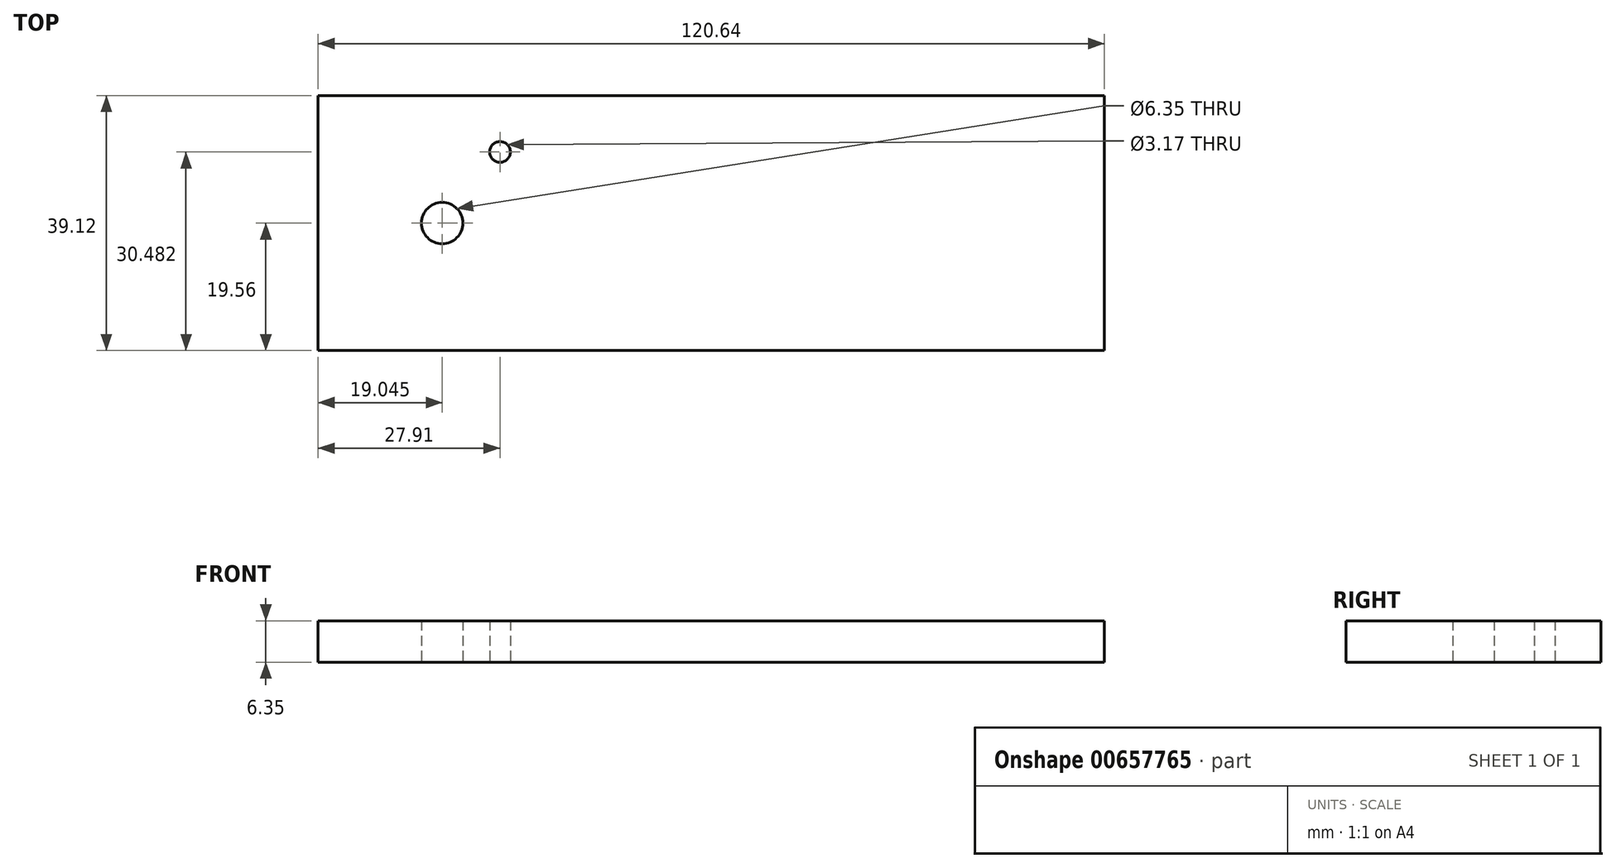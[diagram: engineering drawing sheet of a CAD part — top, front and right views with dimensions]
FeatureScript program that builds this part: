
annotation { "Feature Type Name" : "Feature", "Feature Type Description" : "" }
export const myFeature = defineFeature(function(context is Context, id is Id, definition is map)
    precondition{}
    {
        {
            var Q0;
            Q0=qCreatedBy(makeId("Top.planeOp"),FACE);
            var sketch = newSketch(context, id + "F0", { "sketchPlane" : qUnion([Q0])});
            skLineSegment(sketch, "E0.bottom", {"start": v(60.33, 19.56) * mm, "end": v(-60.33, 19.56) * mm});
            skLineSegment(sketch, "E0.top", {"start": v(60.32, -19.56) * mm, "end": v(-60.33, -19.56) * mm});
            skLineSegment(sketch, "E0.left", {"start": v(60.33, 19.56) * mm, "end": v(60.32, -19.56) * mm});
            skLineSegment(sketch, "E0.right", {"start": v(-60.33, 19.56) * mm, "end": v(-60.33, -19.56) * mm});
            skPoint(sketch, "E0.middle", {"position": v(0, 0) * mm});
            skLineSegment(sketch, "E1", {"start": v(-60.33, 0) * mm, "end": v(60.33, 0) * mm});
            skPoint(sketch, "E2", {"position": v(-41.28, 0) * mm});
            skPoint(sketch, "E3", {"position": v(-32.41, 10.92) * mm});
            skCircle(sketch, "E4", {"center": v(-41.28, 0) * mm, "radius": 3.18 * mm});
            skCircle(sketch, "E5", {"center": v(-32.41, 10.92) * mm, "radius": 1.59 * mm});
            skSolve(sketch);
        }
        {
            var Q0;
            {var subQ1=sQuery(id+"F0.wireOp",EDGE,"E0.top");Q0=makeQuery(id+"F0.imprint","IMPRINT",FACE,{"disambiguationData":[TD([[makeQuery(id+"F0.imprint","IMPRINT",EDGE,{"derivedFrom":subQ1}),-1.0]])]});}
            var Q1;
            {var subQ5=sQuery(id+"F0.wireOp",EDGE,"E0.bottom");Q1=makeQuery(id+"F0.imprint","IMPRINT",FACE,{"disambiguationData":[TD([[makeQuery(id+"F0.imprint","IMPRINT",EDGE,{"derivedFrom":subQ5}),1.0]])]});}
            extrude(context, id + "F1", {"entities" : qUnion([Q0, Q1]), "depth" : 6.35 * mm, "offsetDistance" : 25.4 * mm});
        }
    });
